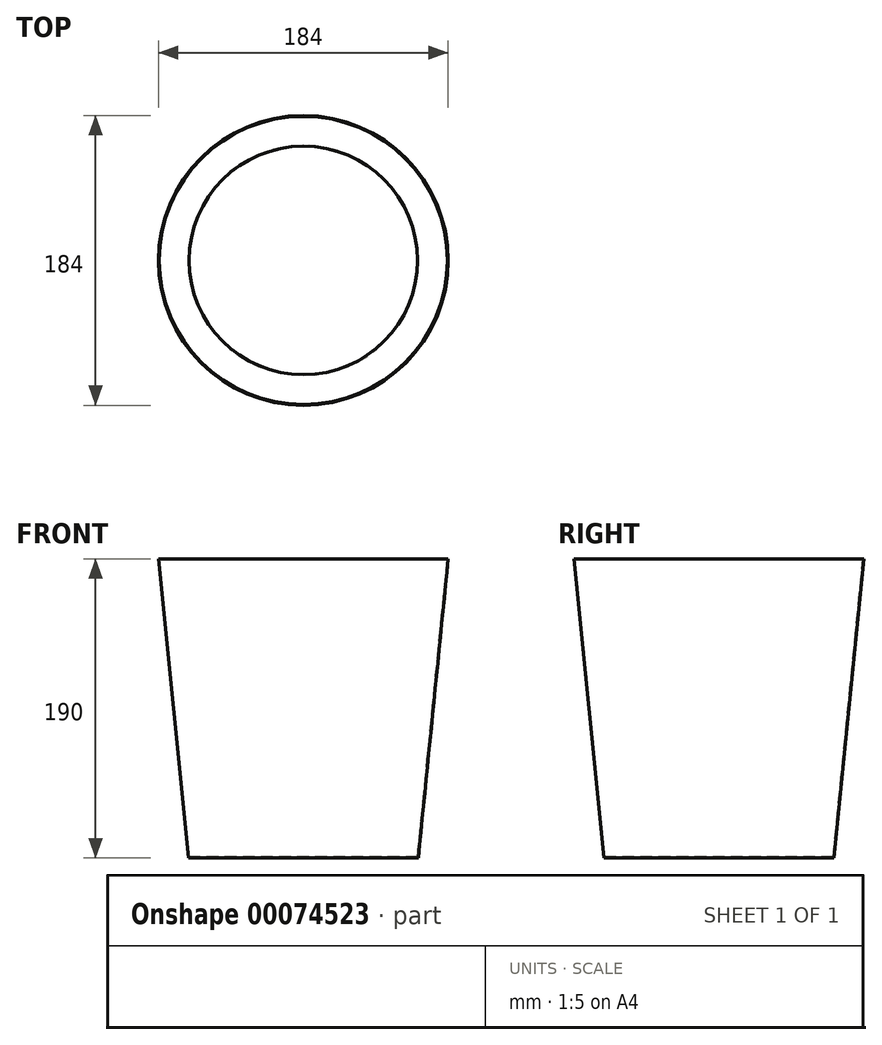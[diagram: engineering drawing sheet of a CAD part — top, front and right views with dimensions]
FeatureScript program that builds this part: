
annotation { "Feature Type Name" : "Feature", "Feature Type Description" : "" }
export const myFeature = defineFeature(function(context is Context, id is Id, definition is map)
    precondition{}
    {
        {
            var Q0;
            Q0=qCreatedBy(makeId("Top.planeOp"),FACE);
            var sketch = newSketch(context, id + "F0", { "sketchPlane" : qUnion([Q0])});
            skCircle(sketch, "E0", {"center": v(0, 0) * mm, "radius": 73 * mm});
            skSolve(sketch);
        }
        {
            var Q0;
            Q0=qCreatedBy(makeId("Top.planeOp"),FACE);
            cPlane(context, id + "F1", {"entities" : qUnion([Q0]), "cplaneType" : CPlaneType.OFFSET, "offset" : 190 * mm, "width" : 150 * mm, "height" : 150 * mm});
        }
        {
            var Q0;
            Q0=qCreatedBy(id+"F1.planeOp",FACE);
            var sketch = newSketch(context, id + "F2", { "sketchPlane" : qUnion([Q0])});
            skCircle(sketch, "E1", {"center": v(0, 0) * mm, "radius": 92 * mm});
            skSolve(sketch);
        }
        {
            var Q0;
            Q0=makeQuery(id+"F2.imprint","IMPRINT",FACE,{"disambiguationData":[TD([[makeQuery(id+"F2.imprint","IMPRINT",EDGE,{"derivedFrom":sQuery(id+"F2.wireOp",EDGE,"E1")}),1.0]])]});
            var Q1;
            Q1=makeQuery(id+"F0.imprint","IMPRINT",FACE,{"disambiguationData":[TD([[makeQuery(id+"F0.imprint","IMPRINT",EDGE,{"derivedFrom":sQuery(id+"F0.wireOp",EDGE,"E0")}),1.0]])]});
            loft(context, id + "F3", {"sheetProfilesArray" : [{ "sheetProfileEntities" : qUnion([Q0]) }, { "sheetProfileEntities" : qUnion([Q1]) }]});
        }
        {
            var Q0;
            Q0=makeQuery(id+"F3.opLoft","CAP_FACE",FACE,{"disambiguationData":[OSD([makeQuery(id+"F2.imprint","IMPRINT",FACE,{"disambiguationData":[TD([[makeQuery(id+"F2.imprint","IMPRINT",EDGE,{"derivedFrom":sQuery(id+"F2.wireOp",EDGE,"E1")}),1.0]])]})])],"isStart":true});
            shell(context, id + "F4", {"entities" : qUnion([Q0]), "thickness" : .5 * mm});
        }
    });
